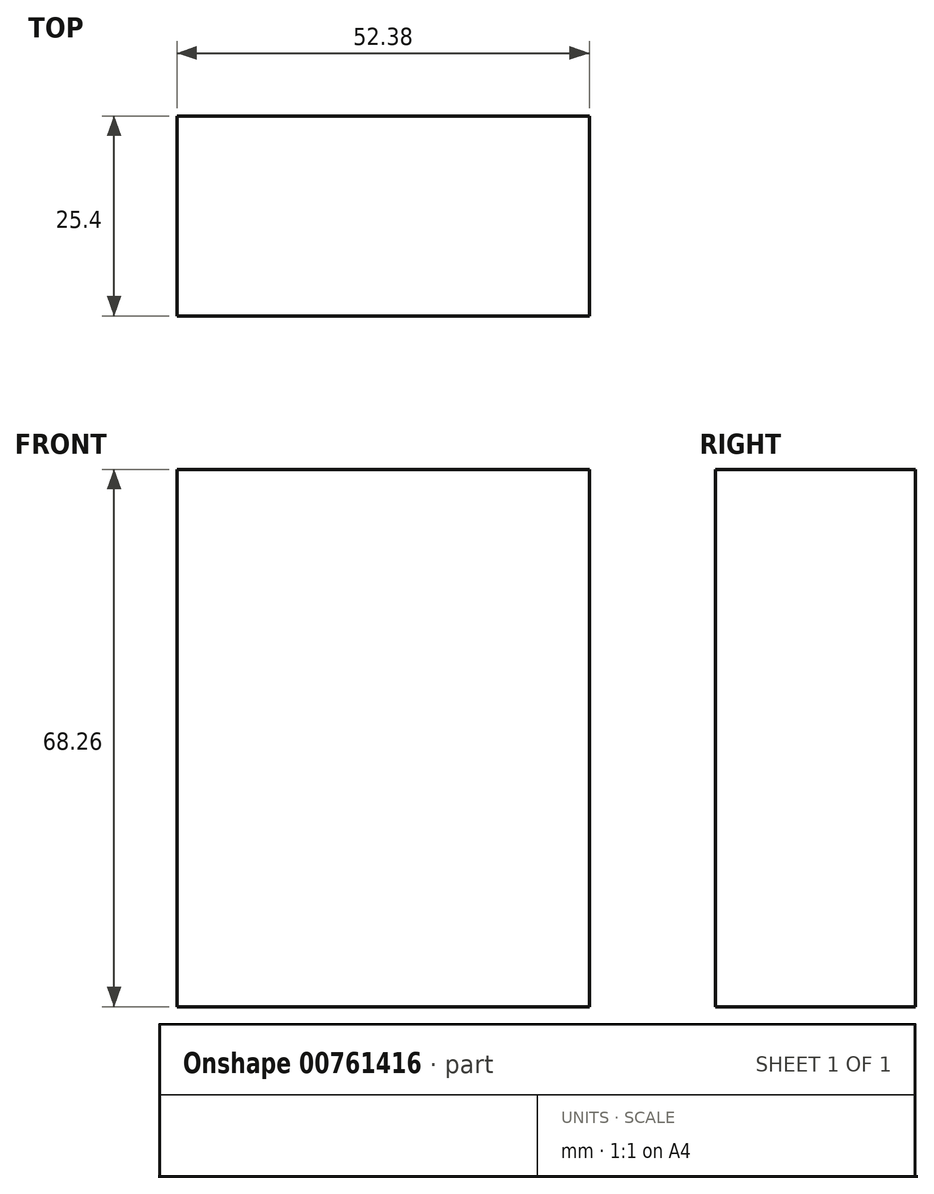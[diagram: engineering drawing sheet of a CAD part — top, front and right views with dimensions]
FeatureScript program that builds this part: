
annotation { "Feature Type Name" : "Feature", "Feature Type Description" : "" }
export const myFeature = defineFeature(function(context is Context, id is Id, definition is map)
    precondition{}
    {
        {
            var Q0;
            Q0=qCreatedBy(makeId("Front.planeOp"),FACE);
            var sketch = newSketch(context, id + "F0", { "sketchPlane" : qUnion([Q0])});
            skLineSegment(sketch, "E0.bottom", {"start": v(26.2, -34.13) * mm, "end": v(-26.2, -34.13) * mm});
            skLineSegment(sketch, "E0.top", {"start": v(26.2, 34.13) * mm, "end": v(-26.2, 34.13) * mm});
            skLineSegment(sketch, "E0.left", {"start": v(26.2, -34.13) * mm, "end": v(26.2, 34.13) * mm});
            skLineSegment(sketch, "E0.right", {"start": v(-26.2, -34.13) * mm, "end": v(-26.2, 34.13) * mm});
            skPoint(sketch, "E0.middle", {"position": v(0, 0) * mm});
            skSolve(sketch);
        }
        {
            var Q0;
            Q0 = qSketchRegion(id + "F0", true);
            extrude(context, id + "F1", {"entities" : qUnion([Q0]), "depth" : 25.4 * mm, "offsetDistance" : 25.4 * mm});
        }
    });
